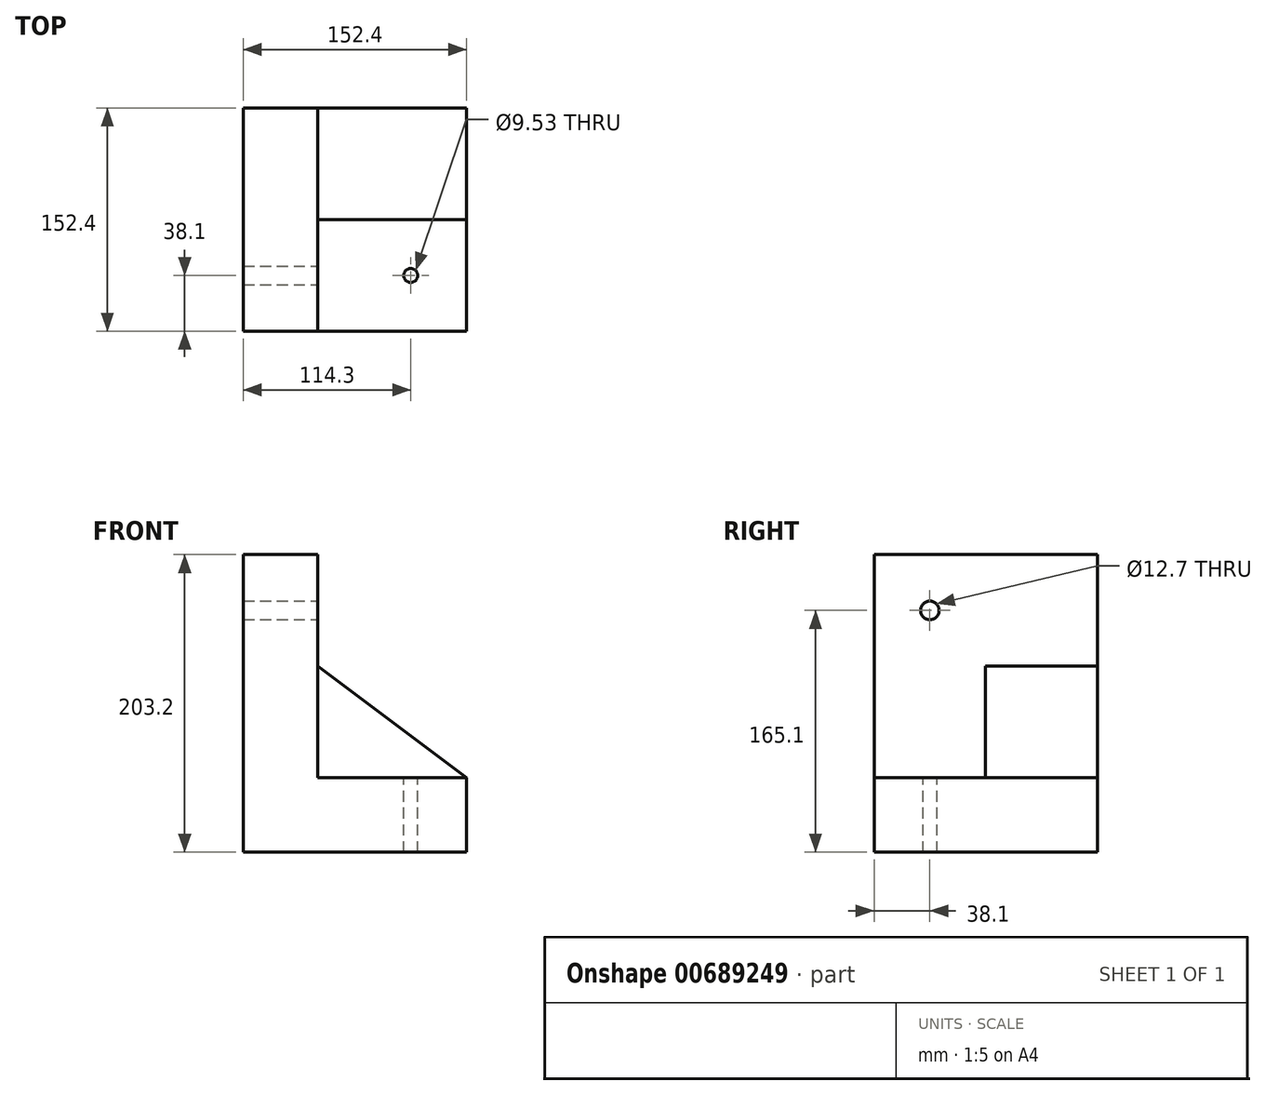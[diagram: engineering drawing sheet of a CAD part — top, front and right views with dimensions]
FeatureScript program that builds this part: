
annotation { "Feature Type Name" : "Feature", "Feature Type Description" : "" }
export const myFeature = defineFeature(function(context is Context, id is Id, definition is map)
    precondition{}
    {
        {
            var Q0;
            Q0=qCreatedBy(makeId("Front.planeOp"),FACE);
            var sketch = newSketch(context, id + "F0", { "sketchPlane" : qUnion([Q0])});
            skLineSegment(sketch, "E0", {"start": v(-50.8, 152.4) * mm, "end": v(-50.8, -50.8) * mm});
            skLineSegment(sketch, "E1", {"start": v(-50.8, -50.8) * mm, "end": v(101.6, -50.8) * mm});
            skLineSegment(sketch, "E2", {"start": v(101.6, -50.8) * mm, "end": v(101.6, 0) * mm});
            skLineSegment(sketch, "E3", {"start": v(101.6, 0) * mm, "end": v(0, 0) * mm});
            skLineSegment(sketch, "E4", {"start": v(0, 0) * mm, "end": v(0, 152.4) * mm});
            skLineSegment(sketch, "E5", {"start": v(0, 152.4) * mm, "end": v(-50.8, 152.4) * mm});
            skSolve(sketch);
        }
        {
            var Q0;
            Q0 = qSketchRegion(id + "F0", true);
            extrude(context, id + "F1", {"entities" : qUnion([Q0]), "depth" : 152.4 * mm, "offsetDistance" : 25.4 * mm});
        }
        {
            var Q0;
            Q0=makeQuery(id+"F1.opExtrude","SWEPT_FACE",FACE,{"disambiguationData":[OSD([sQuery(id+"F0.wireOp",EDGE,"E3")])]});
            var sketch = newSketch(context, id + "F2", { "sketchPlane" : qUnion([Q0])});
            skLineSegment(sketch, "E6.bottom", {"start": v(0, 0) * mm, "end": v(101.6, 0) * mm});
            skLineSegment(sketch, "E6.top", {"start": v(0, -76.2) * mm, "end": v(101.6, -76.2) * mm});
            skLineSegment(sketch, "E6.left", {"start": v(0, 0) * mm, "end": v(0, -76.2) * mm});
            skLineSegment(sketch, "E6.right", {"start": v(101.6, 0) * mm, "end": v(101.6, -76.2) * mm});
            skSolve(sketch);
        }
        {
            var Q0;
            Q0 = qSketchRegion(id + "F2", true);
            var Q1;
            Q1=makeQuery(id+"F2.imprint","IMPRINT",FACE,{"disambiguationData":[TD([[makeQuery(id+"F2.imprint","IMPRINT",EDGE,{"derivedFrom":sQuery(id+"F2.wireOp",EDGE,"E6.bottom")}),1.0]])]});
            extrude(context, id + "F3", {"entities" : qUnion([Q0, Q1]), "operationType" : NewBodyOperationType.ADD, "depth" : 76.2 * mm, "offsetDistance" : 25.4 * mm});
        }
        {
            var Q0;
            Q0=makeQuery(id+"F3.opExtrude","SWEPT_FACE",FACE,{"disambiguationData":[OSD([sQuery(id+"F2.wireOp",EDGE,"E6.top")])]});
            var sketch = newSketch(context, id + "F4", { "sketchPlane" : qUnion([Q0])});
            skLineSegment(sketch, "E7", {"start": v(0, 76.2) * mm, "end": v(101.6, 0) * mm});
            skLineSegment(sketch, "E8", {"start": v(0, 76.2) * mm, "end": v(101.6, 76.2) * mm});
            skLineSegment(sketch, "E9", {"start": v(101.6, 76.2) * mm, "end": v(101.6, 0) * mm});
            skSolve(sketch);
        }
        {
            var Q0;
            Q0=makeQuery(id+"F4.imprint","IMPRINT",FACE,{"disambiguationData":[TD([[makeQuery(id+"F4.imprint","IMPRINT",EDGE,{"derivedFrom":sQuery(id+"F4.wireOp",EDGE,"E7")}),1.0]])]});
            extrude(context, id + "F5", {"entities" : qUnion([Q0]), "operationType" : NewBodyOperationType.REMOVE, "oppositeDirection" : true, "depth" : 76.2 * mm, "offsetDistance" : 25.4 * mm});
        }
        {
            var Q0;
            Q0=makeQuery(id+"F1.opExtrude","SWEPT_FACE",FACE,{"disambiguationData":[OSD([sQuery(id+"F0.wireOp",EDGE,"E4")])]});
            var sketch = newSketch(context, id + "F6", { "sketchPlane" : qUnion([Q0])});
            skCircle(sketch, "E10", {"center": v(-114.3, 114.3) * mm, "radius": 4.76 * mm});
            skSolve(sketch);
        }
        {
            var Q0;
            Q0=sQuery(id+"F6.wireOp",VERTEX,"E10.center");
            var Q1;
            Q1=makeQuery(id+"F1.opExtrude","SWEPT_BODY",BODY,{"disambiguationData":[OSD([sQuery(id+"F0.wireOp",EDGE,"E0"),sQuery(id+"F0.wireOp",EDGE,"E1"),sQuery(id+"F0.wireOp",EDGE,"E2"),sQuery(id+"F0.wireOp",EDGE,"E3"),sQuery(id+"F0.wireOp",EDGE,"E4"),sQuery(id+"F0.wireOp",EDGE,"E5")])]});
            hole(context, id + "F7", {"style" : HoleStyle.SIMPLE, "endStyle" : HoleEndStyle.THROUGH, "holeDiameter" : 12.7 * mm, "majorDiameter" : 6.35 * mm, "isTappedThrough" : true, "tappedDepth" : 12.7 * mm, "tapClearance" : 3, "locations" : qUnion([Q0]), "scope" : qUnion([Q1])});
        }
        {
            var Q0;
            Q0=makeQuery(id+"F1.opExtrude","SWEPT_FACE",FACE,{"disambiguationData":[OSD([sQuery(id+"F0.wireOp",EDGE,"E3")])]});
            var sketch = newSketch(context, id + "F8", { "sketchPlane" : qUnion([Q0])});
            skPoint(sketch, "E11", {"position": v(63.5, -114.3) * mm});
            skSolve(sketch);
        }
        {
            var Q0;
            Q0=sQuery(id+"F8.wireOp",VERTEX,"E11");
            var Q1;
            Q1=makeQuery(id+"F1.opExtrude","SWEPT_BODY",BODY,{"disambiguationData":[OSD([sQuery(id+"F0.wireOp",EDGE,"E0"),sQuery(id+"F0.wireOp",EDGE,"E1"),sQuery(id+"F0.wireOp",EDGE,"E2"),sQuery(id+"F0.wireOp",EDGE,"E3"),sQuery(id+"F0.wireOp",EDGE,"E4"),sQuery(id+"F0.wireOp",EDGE,"E5")])]});
            hole(context, id + "F9", {"style" : HoleStyle.SIMPLE, "endStyle" : HoleEndStyle.THROUGH, "holeDiameter" : 9.52 * mm, "majorDiameter" : 6.35 * mm, "isTappedThrough" : true, "tappedDepth" : 12.7 * mm, "tapClearance" : 3, "locations" : qUnion([Q0]), "scope" : qUnion([Q1])});
        }
    });
